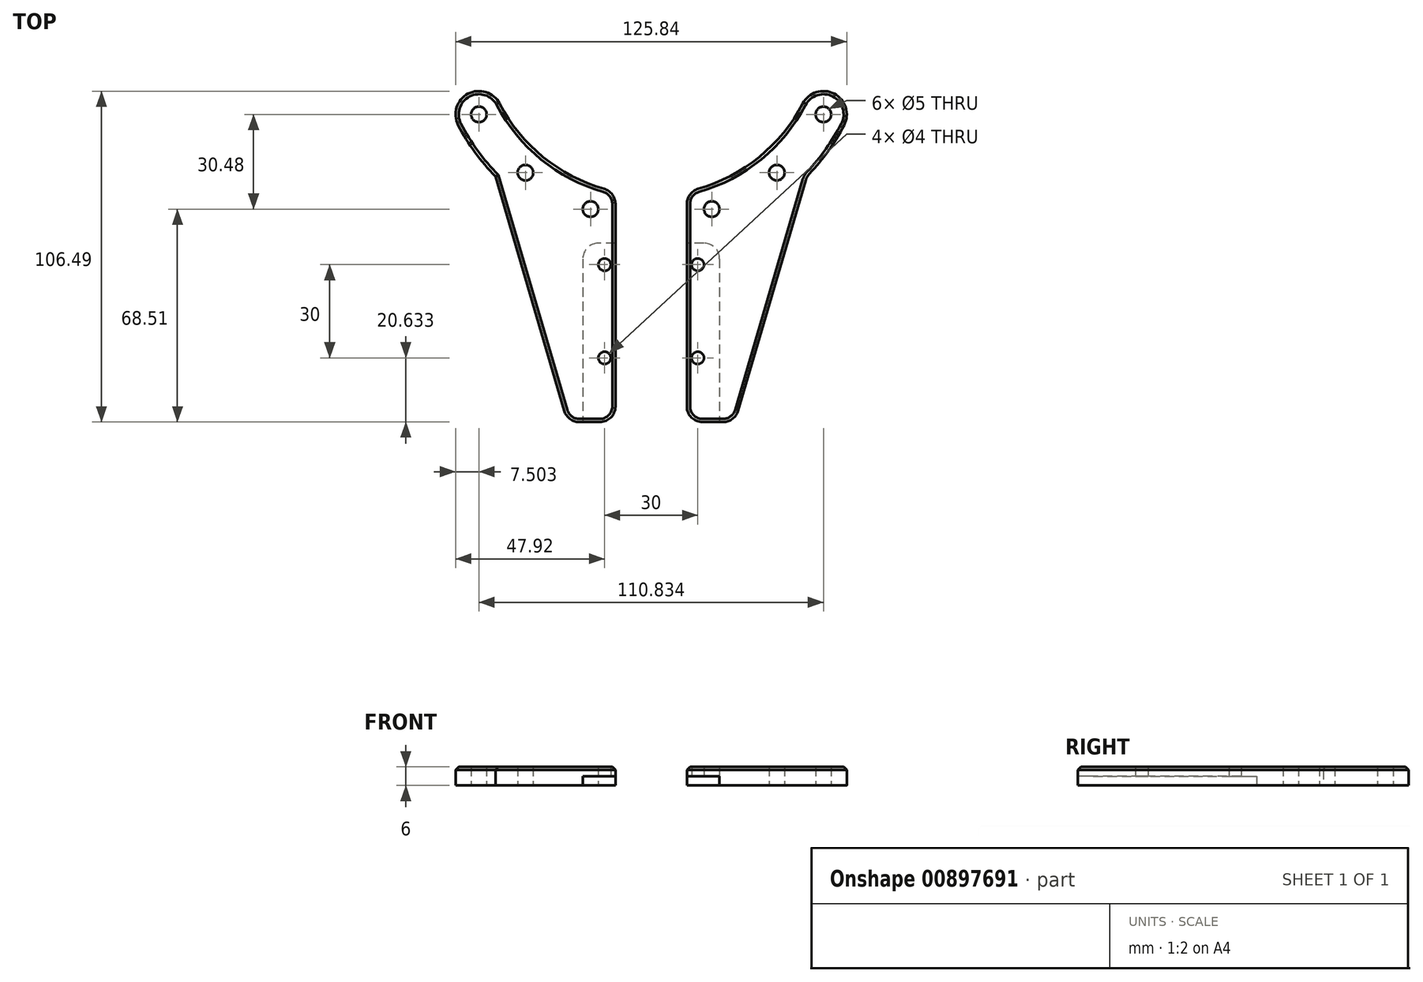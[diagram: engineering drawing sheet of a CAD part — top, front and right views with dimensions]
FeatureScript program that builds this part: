
annotation { "Feature Type Name" : "Feature", "Feature Type Description" : "" }
export const myFeature = defineFeature(function(context is Context, id is Id, definition is map)
    precondition{}
    {
        {
            var Q0;
            Q0=qCreatedBy(makeId("Top.planeOp"),FACE);
            var sketch = newSketch(context, id + "F0", { "sketchPlane" : qUnion([Q0])});
            skLineSegment(sketch, "E0", {"start": v(0, 66.9) * mm, "end": v(0, -103.92) * mm, "construction": true});
            skLineSegment(sketch, "E1", {"start": v(-96.3, 0) * mm, "end": v(93.92, 0) * mm, "construction": true});
            skArc(sketch, "E2", {"start": v(-62.07, -32.37) * mm, "mid": v(-56.68, -41.07) * mm, "end": v(-50.09, -48.9) * mm});
            skArc(sketch, "E3", {"start": v(-48.77, -25.43) * mm, "mid": v(-33.3, -43.77) * mm, "end": v(-11.5, -53.78) * mm});
            skLineSegment(sketch, "E4", {"start": v(-11.5, -69.05) * mm, "end": v(-11.5, -127.9) * mm});
            skLineSegment(sketch, "E5", {"start": v(-11.5, -127.9) * mm, "end": v(-26.89, -127.9) * mm});
            skLineSegment(sketch, "E6", {"start": v(-26.89, -127.9) * mm, "end": v(-50.09, -48.9) * mm});
            skCircle(sketch, "E7", {"center": v(0, 0) * mm, "radius": 62.5 * mm, "construction": true});
            skArc(sketch, "E8", {"start": v(-48.77, -25.43) * mm, "mid": v(-58.88, -22.25) * mm, "end": v(-62.07, -32.37) * mm});
            skPoint(sketch, "E9.orphan", {"position": v(-55, 0) * mm});
            skPoint(sketch, "E10.orphan", {"position": v(-70, 0) * mm});
            skLineSegment(sketch, "E11", {"start": v(-11.5, -69.05) * mm, "end": v(-11.5, -53.78) * mm});
            skCircle(sketch, "E12", {"center": v(-19.5, -59.38) * mm, "radius": 2.5 * mm});
            skCircle(sketch, "E13", {"center": v(-55.42, -28.9) * mm, "radius": 2.5 * mm});
            skCircle(sketch, "E14", {"center": v(-40.44, -47.65) * mm, "radius": 2.5 * mm});
            skCircle(sketch, "E15", {"center": v(-15, -77.26) * mm, "radius": 2 * mm});
            skLineSegment(sketch, "E16.MirrorCS", {"start": v(11.5, -127.9) * mm, "end": v(26.89, -127.9) * mm});
            skArc(sketch, "E17.MirrorCS", {"start": v(62.07, -32.37) * mm, "mid": v(56.68, -41.07) * mm, "end": v(50.09, -48.9) * mm});
            skCircle(sketch, "E18.MirrorC", {"center": v(55.42, -28.9) * mm, "radius": 2.5 * mm});
            skCircle(sketch, "E19.MirrorC", {"center": v(19.5, -59.38) * mm, "radius": 2.5 * mm});
            skArc(sketch, "E20.MirrorCS", {"start": v(48.77, -25.43) * mm, "mid": v(33.3, -43.77) * mm, "end": v(11.5, -53.78) * mm});
            skCircle(sketch, "E21.MirrorC", {"center": v(15, -77.26) * mm, "radius": 2 * mm});
            skCircle(sketch, "E22.MirrorC", {"center": v(40.44, -47.65) * mm, "radius": 2.5 * mm});
            skLineSegment(sketch, "E23.MirrorCS", {"start": v(11.5, -69.05) * mm, "end": v(11.5, -127.9) * mm});
            skArc(sketch, "E24.MirrorCS", {"start": v(48.77, -25.43) * mm, "mid": v(58.88, -22.25) * mm, "end": v(62.07, -32.37) * mm});
            skLineSegment(sketch, "E25.MirrorCS", {"start": v(11.5, -69.05) * mm, "end": v(11.5, -53.78) * mm});
            skLineSegment(sketch, "E26.MirrorCS", {"start": v(26.89, -127.9) * mm, "end": v(50.09, -48.9) * mm});
            skLineSegment(sketch, "E27", {"start": v(-15, -77.26) * mm, "end": v(-15, -107.26) * mm, "construction": true});
            skCircle(sketch, "E28", {"center": v(-15, -107.26) * mm, "radius": 2 * mm});
            skCircle(sketch, "E29.MirrorC", {"center": v(15, -107.26) * mm, "radius": 2 * mm});
            skSolve(sketch);
        }
        {
            var Q0;
            Q0 = qSketchRegion(id + "F0", true);
            extrude(context, id + "F1", {"entities" : qUnion([Q0]), "depth" : 6 * mm, "offsetDistance" : 25 * mm});
        }
        {
            var Q0;
            Q0=makeQuery(id+"F1.opExtrude","SWEPT_EDGE",EDGE,{"disambiguationData":[OSD([sQuery(id+"F0.wireOp",EDGE,"E5"),sQuery(id+"F0.wireOp",EDGE,"E6")])]});
            var Q1;
            Q1=makeQuery(id+"F1.opExtrude","SWEPT_EDGE",EDGE,{"disambiguationData":[OSD([sQuery(id+"F0.wireOp",EDGE,"E4"),sQuery(id+"F0.wireOp",EDGE,"E5")])]});
            var Q2;
            Q2=makeQuery(id+"F1.opExtrude","SWEPT_EDGE",EDGE,{"disambiguationData":[OSD([sQuery(id+"F0.wireOp",EDGE,"E3"),sQuery(id+"F0.wireOp",EDGE,"E11")])]});
            var Q3;
            Q3=makeQuery(id+"F1.opExtrude","SWEPT_EDGE",EDGE,{"disambiguationData":[OSD([sQuery(id+"F0.wireOp",EDGE,"E20.MirrorCS"),sQuery(id+"F0.wireOp",EDGE,"E25.MirrorCS")])]});
            var Q4;
            Q4=makeQuery(id+"F1.opExtrude","SWEPT_EDGE",EDGE,{"disambiguationData":[OSD([sQuery(id+"F0.wireOp",EDGE,"E16.MirrorCS"),sQuery(id+"F0.wireOp",EDGE,"E23.MirrorCS")])]});
            var Q5;
            Q5=makeQuery(id+"F1.opExtrude","SWEPT_EDGE",EDGE,{"disambiguationData":[OSD([sQuery(id+"F0.wireOp",EDGE,"E16.MirrorCS"),sQuery(id+"F0.wireOp",EDGE,"E26.MirrorCS")])]});
            var Q6;
            Q6=makeQuery(id+"F1.opExtrude","SWEPT_EDGE",EDGE,{"disambiguationData":[OSD([sQuery(id+"F0.wireOp",EDGE,"E17.MirrorCS"),sQuery(id+"F0.wireOp",EDGE,"E26.MirrorCS")])]});
            fillet(context, id + "F2", {"entities" : qUnion([Q0, Q1, Q2, Q3, Q4, Q5, Q6]), "radius" : 5 * mm, "tangentPropagation" : true, "allowEdgeOverflow" : false});
        }
        {
            var Q0;
            {var subQ0=sQuery(id+"F0.wireOp",EDGE,"E5");var subQ1=sQuery(id+"F0.wireOp",EDGE,"E4");Q0=makeQuery(id+"F2.opFillet","BLEND_EDGE",EDGE,{"blendedFrom":[makeQuery(id+"F1.opExtrude","SWEPT_EDGE",EDGE,{"disambiguationData":[OSD([subQ1,subQ0])]}),makeQuery(id+"F1.opExtrude","CAP_FACE",FACE,{"disambiguationData":[OSD([sQuery(id+"F0.wireOp",EDGE,"E2"),sQuery(id+"F0.wireOp",EDGE,"E3"),subQ1,subQ0,sQuery(id+"F0.wireOp",EDGE,"E6"),sQuery(id+"F0.wireOp",EDGE,"E8"),sQuery(id+"F0.wireOp",EDGE,"E11"),sQuery(id+"F0.wireOp",EDGE,"E12"),sQuery(id+"F0.wireOp",EDGE,"E13"),sQuery(id+"F0.wireOp",EDGE,"E14"),sQuery(id+"F0.wireOp",EDGE,"E15"),sQuery(id+"F0.wireOp",EDGE,"E28")])],"isStart":false})],"blendedInto":[makeQuery(id+"F1.opExtrude","CAP_FACE",FACE,{"disambiguationData":[OSD([sQuery(id+"F0.wireOp",EDGE,"E2"),sQuery(id+"F0.wireOp",EDGE,"E3"),subQ1,subQ0,sQuery(id+"F0.wireOp",EDGE,"E6"),sQuery(id+"F0.wireOp",EDGE,"E8"),sQuery(id+"F0.wireOp",EDGE,"E11"),sQuery(id+"F0.wireOp",EDGE,"E12"),sQuery(id+"F0.wireOp",EDGE,"E13"),sQuery(id+"F0.wireOp",EDGE,"E14"),sQuery(id+"F0.wireOp",EDGE,"E15"),sQuery(id+"F0.wireOp",EDGE,"E28")])],"isStart":false})]});}
            var Q1;
            Q1=makeQuery(id+"F1.opExtrude","CAP_EDGE",EDGE,{"disambiguationData":[OSD([sQuery(id+"F0.wireOp",EDGE,"E23.MirrorCS"),sQuery(id+"F0.wireOp",EDGE,"E25.MirrorCS")])],"isStart":false});
            chamfer(context, id + "F3", {"entities" : qUnion([Q0, Q1]), "width" : 1 * mm, "tangentPropagation" : true});
        }
        {
            var Q0;
            Q0=makeQuery(id+"F1.opExtrude","CAP_FACE",FACE,{"disambiguationData":[OSD([sQuery(id+"F0.wireOp",EDGE,"E2"),sQuery(id+"F0.wireOp",EDGE,"E3"),sQuery(id+"F0.wireOp",EDGE,"E4"),sQuery(id+"F0.wireOp",EDGE,"E5"),sQuery(id+"F0.wireOp",EDGE,"E6"),sQuery(id+"F0.wireOp",EDGE,"E8"),sQuery(id+"F0.wireOp",EDGE,"E11"),sQuery(id+"F0.wireOp",EDGE,"E12"),sQuery(id+"F0.wireOp",EDGE,"E13"),sQuery(id+"F0.wireOp",EDGE,"E14"),sQuery(id+"F0.wireOp",EDGE,"E15"),sQuery(id+"F0.wireOp",EDGE,"E28")])],"isStart":true});
            var sketch = newSketch(context, id + "F4", { "sketchPlane" : qUnion([Q0])});
            skLineSegment(sketch, "E30", {"start": v(0, 39.64) * mm, "end": v(0, 253.32) * mm, "construction": true});
            skLineSegment(sketch, "E31.bottom", {"start": v(22, 70.36) * mm, "end": v(-22, 70.36) * mm});
            skLineSegment(sketch, "E31.top", {"start": v(22, 150.36) * mm, "end": v(-22, 150.36) * mm});
            skLineSegment(sketch, "E31.left", {"start": v(22, 70.36) * mm, "end": v(22, 150.36) * mm});
            skLineSegment(sketch, "E31.right", {"start": v(-22, 70.36) * mm, "end": v(-22, 150.36) * mm});
            skPoint(sketch, "E31.middle", {"position": v(0, 110.36) * mm});
            skPoint(sketch, "E32", {"position": v(0, 146.48) * mm});
            skSolve(sketch);
        }
        {
            var Q0;
            Q0 = qSketchRegion(id + "F4", true);
            extrude(context, id + "F5", {"entities" : qUnion([Q0]), "operationType" : NewBodyOperationType.REMOVE, "oppositeDirection" : true, "depth" : 3 * mm, "offsetDistance" : 25 * mm});
        }
        {
            var Q0;
            Q0=makeQuery(id+"F5.boolean.opBoolean","COPY",EDGE,{"derivedFrom":makeQuery(id+"F5.opExtrude","SWEPT_EDGE",EDGE,{"disambiguationData":[OSD([sQuery(id+"F4.wireOp",EDGE,"E31.bottom"),sQuery(id+"F4.wireOp",EDGE,"E31.left")])]})});
            var Q1;
            Q1=makeQuery(id+"F5.boolean.opBoolean","COPY",EDGE,{"derivedFrom":makeQuery(id+"F5.opExtrude","SWEPT_EDGE",EDGE,{"disambiguationData":[OSD([sQuery(id+"F4.wireOp",EDGE,"E31.bottom"),sQuery(id+"F4.wireOp",EDGE,"E31.right")])]})});
            fillet(context, id + "F6", {"entities" : qUnion([Q0, Q1]), "radius" : 5 * mm, "tangentPropagation" : true, "allowEdgeOverflow" : false});
        }
    });
